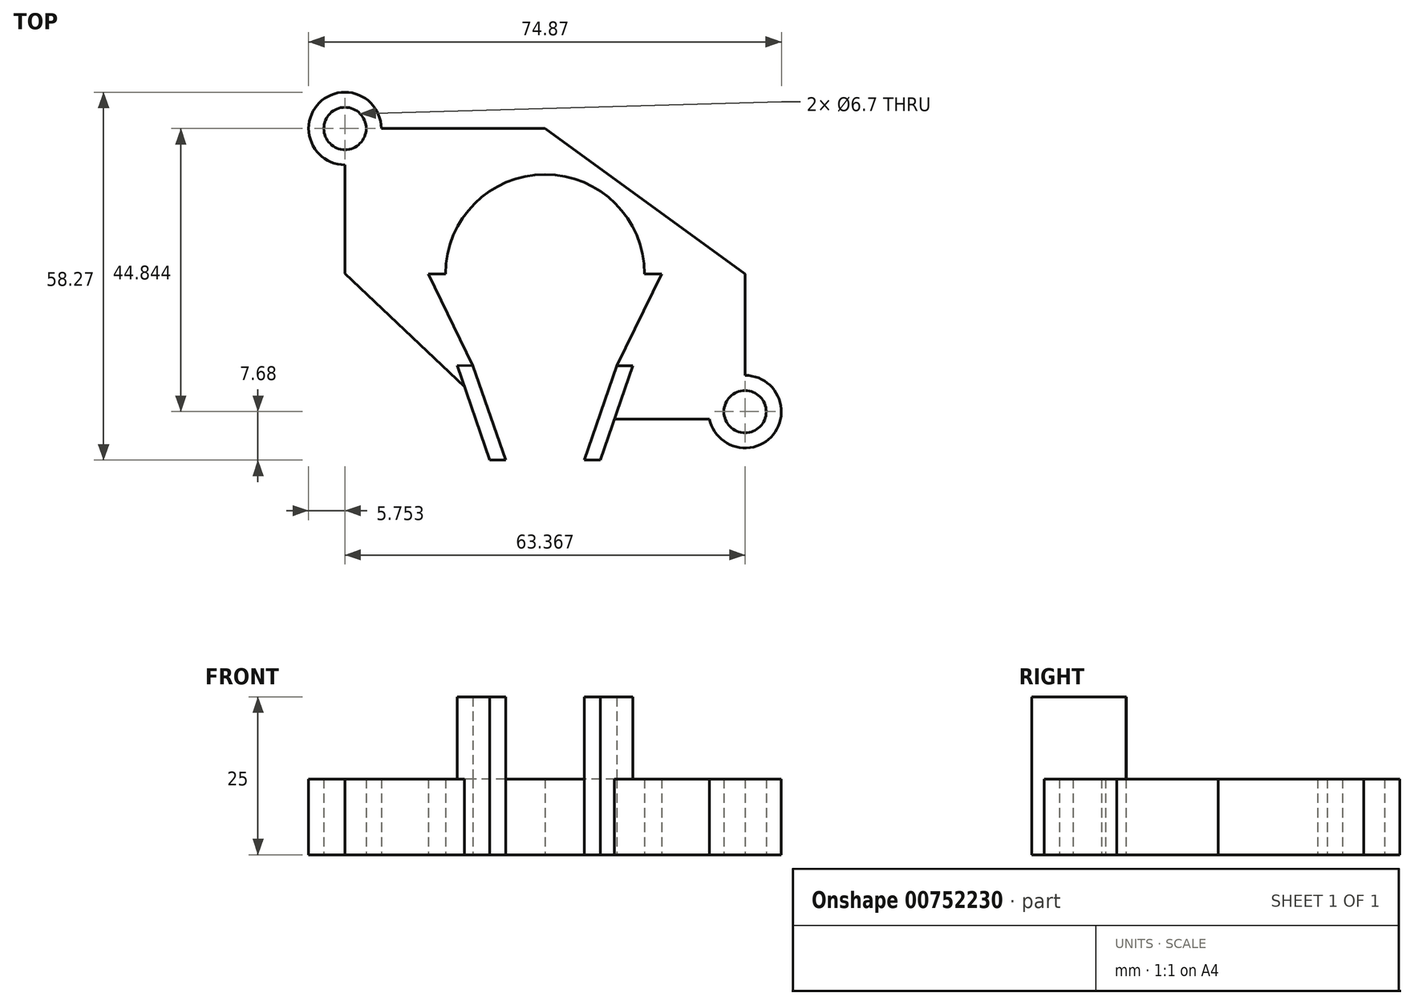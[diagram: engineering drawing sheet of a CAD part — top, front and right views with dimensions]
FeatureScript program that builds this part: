
annotation { "Feature Type Name" : "Feature", "Feature Type Description" : "" }
export const myFeature = defineFeature(function(context is Context, id is Id, definition is map)
    precondition{}
    {
        {
            var Q0;
            Q0=qCreatedBy(makeId("Top.planeOp"),FACE);
            var sketch = newSketch(context, id + "F0", { "sketchPlane" : qUnion([Q0])});
            skLineSegment(sketch, "E0.bottom", {"start": v(-52.47, 38.18) * mm, "end": v(4.2, 38.18) * mm});
            skLineSegment(sketch, "E0.left", {"start": v(-55.82, 34.83) * mm, "end": v(-55.82, -4.47) * mm});
            skLineSegment(sketch, "E0.right", {"start": v(7.55, 34.83) * mm, "end": v(7.55, -3.3) * mm});
            skCircle(sketch, "E1", {"center": v(7.55, 38.18) * mm, "radius": 3.35 * mm});
            skCircle(sketch, "E2", {"center": v(-55.82, 38.18) * mm, "radius": 3.35 * mm});
            skCircle(sketch, "E3", {"center": v(-55.82, -7.82) * mm, "radius": 3.35 * mm});
            skCircle(sketch, "E4", {"center": v(7.55, -6.66) * mm, "radius": 3.35 * mm});
            skCircle(sketch, "E5", {"center": v(-55.82, 38.18) * mm, "radius": 5.75 * mm});
            skCircle(sketch, "E6", {"center": v(7.55, 38.18) * mm, "radius": 5.75 * mm});
            skCircle(sketch, "E7", {"center": v(7.55, -6.66) * mm, "radius": 5.75 * mm});
            skCircle(sketch, "E8", {"center": v(-55.82, -7.82) * mm, "radius": 5.75 * mm});
            skPoint(sketch, "E9.first.point", {"position": v(-24.13, 38.18) * mm});
            skPoint(sketch, "E9.second.point", {"position": v(-55.82, 15.18) * mm});
            skPoint(sketch, "E10.middle", {"position": v(-24.13, 15.17) * mm});
            skCircle(sketch, "E11", {"center": v(-24.13, 15.17) * mm, "radius": 15.75 * mm});
            skArc(sketch, "E12", {"start": v(-5.63, 15.17) * mm, "mid": v(-24.13, 33.67) * mm, "end": v(-42.63, 15.17) * mm});
            skLineSegment(sketch, "E13", {"start": v(-24.13, -7.82) * mm, "end": v(-24.13, -7.85) * mm});
            skLineSegment(sketch, "E14", {"start": v(-35.53, 0.6) * mm, "end": v(-30.38, -14.34) * mm});
            skLineSegment(sketch, "E15", {"start": v(-17.88, -14.34) * mm, "end": v(-12.74, 0.6) * mm});
            skLineSegment(sketch, "E16", {"start": v(-30.38, -14.34) * mm, "end": v(-32.88, -14.34) * mm});
            skLineSegment(sketch, "E17", {"start": v(-32.88, -14.34) * mm, "end": v(-38.03, 0.64) * mm});
            skLineSegment(sketch, "E18", {"start": v(-38.03, 0.64) * mm, "end": v(-35.53, 0.6) * mm});
            skLineSegment(sketch, "E19", {"start": v(-17.88, -14.34) * mm, "end": v(-15.38, -14.34) * mm});
            skLineSegment(sketch, "E20", {"start": v(-15.38, -14.34) * mm, "end": v(-10.24, 0.6) * mm});
            skLineSegment(sketch, "E21", {"start": v(-10.24, 0.6) * mm, "end": v(-12.74, 0.6) * mm});
            skLineSegment(sketch, "E22.trimOffspring", {"start": v(-55.82, -7.82) * mm, "end": v(-55.82, -7.85) * mm});
            skLineSegment(sketch, "E23.trimOffspring", {"start": v(7.55, 38.18) * mm, "end": v(7.55, 38.18) * mm});
            skPoint(sketch, "E24.orphan", {"position": v(-24.13, -14.34) * mm});
            skLineSegment(sketch, "E25", {"start": v(-24.13, 15.17) * mm, "end": v(-42.63, 15.17) * mm});
            skLineSegment(sketch, "E26", {"start": v(-35.53, 0.6) * mm, "end": v(-42.63, 15.17) * mm});
            skLineSegment(sketch, "E27", {"start": v(-24.13, 15.17) * mm, "end": v(-5.63, 15.17) * mm});
            skLineSegment(sketch, "E28", {"start": v(-12.74, 0.6) * mm, "end": v(-5.63, 15.17) * mm});
            skLineSegment(sketch, "E29", {"start": v(-30.38, -14.34) * mm, "end": v(-17.88, -14.34) * mm});
            skLineSegment(sketch, "E30", {"start": v(-42.63, 15.17) * mm, "end": v(-55.82, 15.18) * mm});
            skLineSegment(sketch, "E31", {"start": v(-5.63, 15.17) * mm, "end": v(7.55, 15.17) * mm});
            skLineSegment(sketch, "E32", {"start": v(-24.13, 15.17) * mm, "end": v(-24.13, -14.34) * mm});
            skLineSegment(sketch, "E33", {"start": v(-24.13, 15.17) * mm, "end": v(-24.13, 38.18) * mm});
            skLineSegment(sketch, "E34", {"start": v(-35.53, 0.6) * mm, "end": v(-12.74, 0.6) * mm});
            skLineSegment(sketch, "E35", {"start": v(-24.13, -7.82) * mm, "end": v(1.92, -7.82) * mm});
            skLineSegment(sketch, "E36", {"start": v(-24.13, -7.82) * mm, "end": v(-50.07, -7.82) * mm});
            skLineSegment(sketch, "E37", {"start": v(-24.13, 38.18) * mm, "end": v(7.55, 15.17) * mm});
            skLineSegment(sketch, "E38", {"start": v(-55.82, 15.18) * mm, "end": v(-36.88, -2.7) * mm});
            skSolve(sketch);
        }
        {
            var Q0;
            {var subQ0=sQuery(id+"F0.wireOp",EDGE,"E0.bottom");var subQ1=sQuery(id+"F0.wireOp",EDGE,"E2");var subQ2=makeQuery(id+"F0.imprint","INTERSECT",VERTEX,{"derivedFrom":[subQ1,subQ0]});Q0=makeQuery(id+"F0.imprint","IMPRINT",FACE,{"disambiguationData":[TD([[makeQuery(id+"F0.imprint","IMPRINT",EDGE,{"disambiguationData":[TD([[subQ2,-1.0]])],"derivedFrom":subQ1}),-1.0]])]});}
            var Q1;
            {var subQ0=sQuery(id+"F0.wireOp",EDGE,"E0.bottom");var subQ1=sQuery(id+"F0.wireOp",EDGE,"E2");var subQ2=makeQuery(id+"F0.imprint","INTERSECT",VERTEX,{"derivedFrom":[subQ1,subQ0]});Q1=makeQuery(id+"F0.imprint","IMPRINT",FACE,{"disambiguationData":[TD([[makeQuery(id+"F0.imprint","IMPRINT",EDGE,{"disambiguationData":[TD([[subQ2,1.0]])],"derivedFrom":subQ1}),-1.0]])]});}
            var Q2;
            {var subQ0=sQuery(id+"F0.wireOp",EDGE,"E30");Q2=makeQuery(id+"F0.imprint","IMPRINT",FACE,{"disambiguationData":[TD([[makeQuery(id+"F0.imprint","IMPRINT",EDGE,{"derivedFrom":subQ0}),-1.0]])]});}
            var Q3;
            {var subQ0=sQuery(id+"F0.wireOp",EDGE,"E33");var subQ1=sQuery(id+"F0.wireOp",EDGE,"E11");var subQ2=makeQuery(id+"F0.imprint","INTERSECT",VERTEX,{"derivedFrom":[subQ1,subQ0]});Q3=makeQuery(id+"F0.imprint","IMPRINT",FACE,{"disambiguationData":[TD([[makeQuery(id+"F0.imprint","IMPRINT",EDGE,{"disambiguationData":[TD([[subQ2,-1.0]])],"derivedFrom":subQ1}),-1.0]])]});}
            var Q4;
            {var subQ0=sQuery(id+"F0.wireOp",EDGE,"E31");Q4=makeQuery(id+"F0.imprint","IMPRINT",FACE,{"disambiguationData":[TD([[makeQuery(id+"F0.imprint","IMPRINT",EDGE,{"derivedFrom":subQ0}),1.0]])]});}
            var Q5;
            {var subQ0=sQuery(id+"F0.wireOp",EDGE,"E33");var subQ1=sQuery(id+"F0.wireOp",EDGE,"E11");var subQ2=makeQuery(id+"F0.imprint","INTERSECT",VERTEX,{"derivedFrom":[subQ1,subQ0]});Q5=makeQuery(id+"F0.imprint","IMPRINT",FACE,{"disambiguationData":[TD([[makeQuery(id+"F0.imprint","IMPRINT",EDGE,{"disambiguationData":[TD([[subQ2,1.0]])],"derivedFrom":subQ1}),-1.0]])]});}
            var Q6;
            {var subQ0=sQuery(id+"F0.wireOp",EDGE,"E21");Q6=makeQuery(id+"F0.imprint","IMPRINT",FACE,{"disambiguationData":[TD([[makeQuery(id+"F0.imprint","IMPRINT",EDGE,{"derivedFrom":subQ0}),-1.0]])]});}
            var Q7;
            {var subQ0=sQuery(id+"F0.wireOp",EDGE,"E18");Q7=makeQuery(id+"F0.imprint","IMPRINT",FACE,{"disambiguationData":[TD([[makeQuery(id+"F0.imprint","IMPRINT",EDGE,{"derivedFrom":subQ0}),1.0]])]});}
            var Q8;
            Q8=makeQuery(id+"F0.imprint","IMPRINT",FACE,{"disambiguationData":[TD([[makeQuery(id+"F0.imprint","IMPRINT",EDGE,{"derivedFrom":sQuery(id+"F0.wireOp",EDGE,"E4")}),-1.0]])]});
            var Q9;
            {var subQ0=sQuery(id+"F0.wireOp",EDGE,"E18");Q9=makeQuery(id+"F0.imprint","IMPRINT",FACE,{"disambiguationData":[TD([[makeQuery(id+"F0.imprint","IMPRINT",EDGE,{"derivedFrom":subQ0}),-1.0]])]});}
            var Q10;
            {var subQ0=sQuery(id+"F0.wireOp",EDGE,"E16");Q10=makeQuery(id+"F0.imprint","IMPRINT",FACE,{"disambiguationData":[TD([[makeQuery(id+"F0.imprint","IMPRINT",EDGE,{"derivedFrom":subQ0}),-1.0]])]});}
            var Q11;
            {var subQ0=sQuery(id+"F0.wireOp",EDGE,"E19");Q11=makeQuery(id+"F0.imprint","IMPRINT",FACE,{"disambiguationData":[TD([[makeQuery(id+"F0.imprint","IMPRINT",EDGE,{"derivedFrom":subQ0}),1.0]])]});}
            var Q12;
            {var subQ0=sQuery(id+"F0.wireOp",EDGE,"E21");Q12=makeQuery(id+"F0.imprint","IMPRINT",FACE,{"disambiguationData":[TD([[makeQuery(id+"F0.imprint","IMPRINT",EDGE,{"derivedFrom":subQ0}),1.0]])]});}
            extrude(context, id + "F1", {"entities" : qUnion([Q0, Q1, Q2, Q3, Q4, Q5, Q6, Q7, Q8, Q9, Q10, Q11, Q12]), "depth" : 12 * mm, "offsetDistance" : 25 * mm});
        }
        {
            var Q0;
            {var subQ0=sQuery(id+"F0.wireOp",EDGE,"E18");Q0=makeQuery(id+"F0.imprint","IMPRINT",FACE,{"disambiguationData":[TD([[makeQuery(id+"F0.imprint","IMPRINT",EDGE,{"derivedFrom":subQ0}),-1.0]])]});}
            var Q1;
            {var subQ0=sQuery(id+"F0.wireOp",EDGE,"E16");Q1=makeQuery(id+"F0.imprint","IMPRINT",FACE,{"disambiguationData":[TD([[makeQuery(id+"F0.imprint","IMPRINT",EDGE,{"derivedFrom":subQ0}),-1.0]])]});}
            var Q2;
            {var subQ0=sQuery(id+"F0.wireOp",EDGE,"E21");Q2=makeQuery(id+"F0.imprint","IMPRINT",FACE,{"disambiguationData":[TD([[makeQuery(id+"F0.imprint","IMPRINT",EDGE,{"derivedFrom":subQ0}),1.0]])]});}
            var Q3;
            {var subQ0=sQuery(id+"F0.wireOp",EDGE,"E19");Q3=makeQuery(id+"F0.imprint","IMPRINT",FACE,{"disambiguationData":[TD([[makeQuery(id+"F0.imprint","IMPRINT",EDGE,{"derivedFrom":subQ0}),1.0]])]});}
            extrude(context, id + "F2", {"entities" : qUnion([Q0, Q1, Q2, Q3]), "operationType" : NewBodyOperationType.ADD, "depth" : 25 * mm, "offsetDistance" : 25 * mm});
        }
    });
